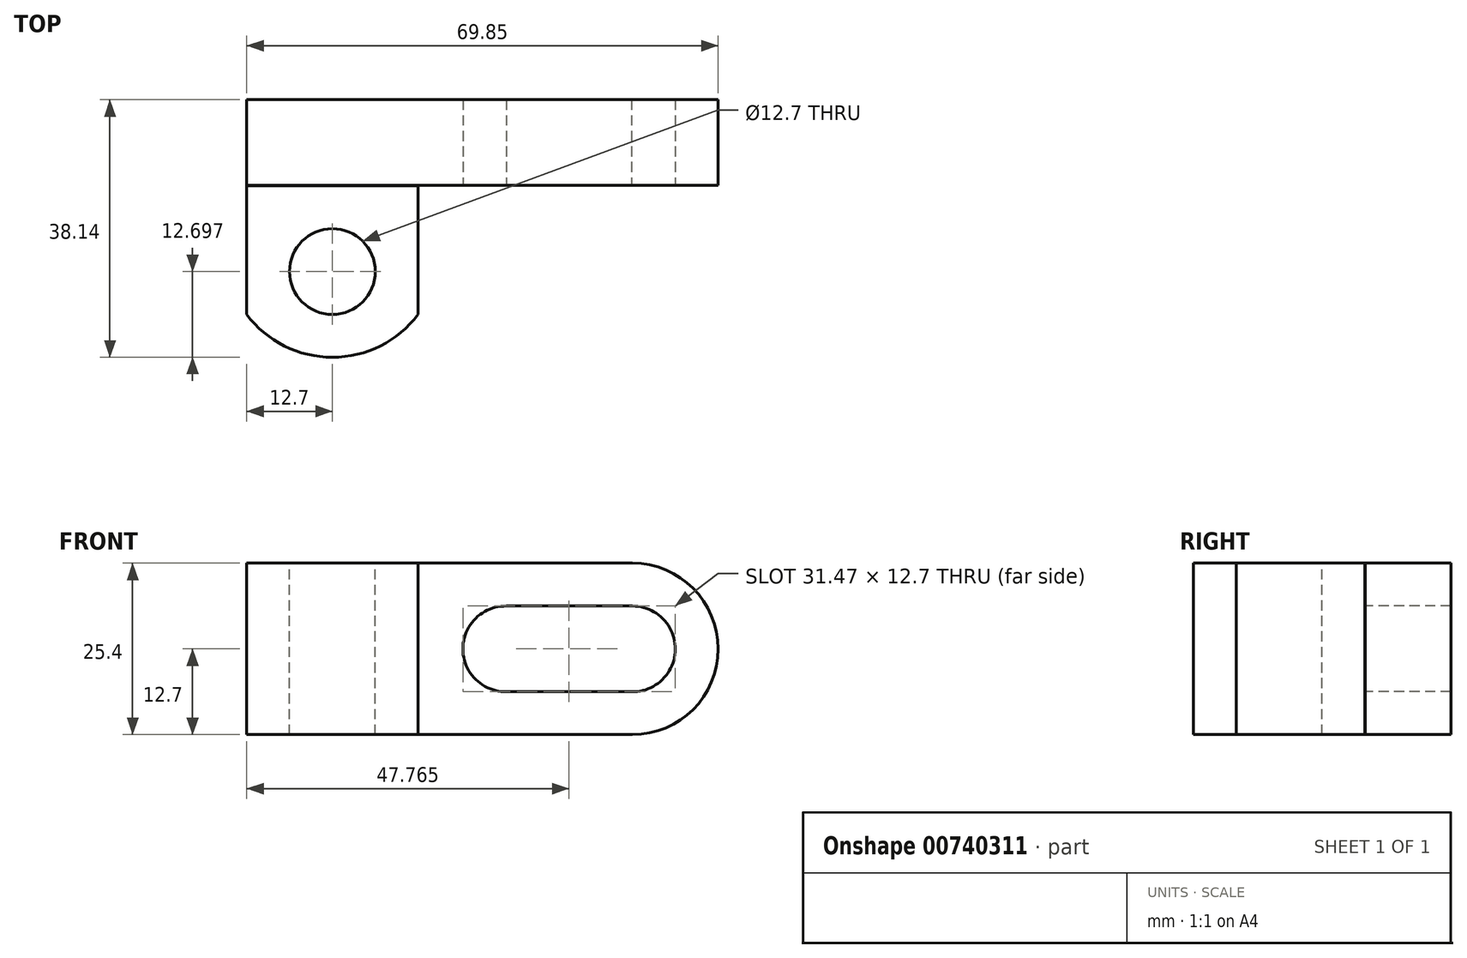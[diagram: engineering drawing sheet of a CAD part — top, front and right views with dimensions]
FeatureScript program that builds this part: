
annotation { "Feature Type Name" : "Feature", "Feature Type Description" : "" }
export const myFeature = defineFeature(function(context is Context, id is Id, definition is map)
    precondition{}
    {
        {
            var Q0;
            Q0=qCreatedBy(makeId("Front.planeOp"),FACE);
            var sketch = newSketch(context, id + "F0", { "sketchPlane" : qUnion([Q0])});
            skCircle(sketch, "E0", {"center": v(57.15, 0) * mm, "radius": 12.7 * mm});
            skLineSegment(sketch, "E1", {"start": v(57.15, 12.7) * mm, "end": v(0, 12.7) * mm});
            skLineSegment(sketch, "E2", {"start": v(0, 12.7) * mm, "end": v(0, -12.7) * mm});
            skLineSegment(sketch, "E3", {"start": v(0, -12.7) * mm, "end": v(57.15, -12.7) * mm});
            skSolve(sketch);
        }
        {
            var Q0;
            Q0 = qSketchRegion(id + "F0", true);
            extrude(context, id + "F1", {"entities" : qUnion([Q0]), "depth" : 12.7 * mm, "offsetDistance" : 25.4 * mm});
        }
        {
            var Q0;
            Q0=qCreatedBy(makeId("Top.planeOp"),FACE);
            var sketch = newSketch(context, id + "F2", { "sketchPlane" : qUnion([Q0])});
            skLineSegment(sketch, "E4", {"start": v(0, -12.74) * mm, "end": v(0, -31.8) * mm});
            skLineSegment(sketch, "E5", {"start": v(0, -31.8) * mm, "end": v(25.4, -31.8) * mm});
            skLineSegment(sketch, "E6", {"start": v(25.4, -31.8) * mm, "end": v(25.4, -12.75) * mm});
            skArc(sketch, "E7", {"start": v(0, -31.8) * mm, "mid": v(12.7, -38.14) * mm, "end": v(25.4, -31.8) * mm});
            skLineSegment(sketch, "E8", {"start": v(0, -12.74) * mm, "end": v(25.4, -12.75) * mm});
            skSolve(sketch);
        }
        {
            var Q0;
            Q0 = qSketchRegion(id + "F2", true);
            extrude(context, id + "F3", {"entities" : qUnion([Q0]), "depth" : 12.7 * mm, "offsetDistance" : 25.4 * mm});
        }
        {
            var Q0;
            Q0=makeQuery(id+"F3.opExtrude","CAP_FACE",FACE,{"disambiguationData":[OSD([sQuery(id+"F2.wireOp",EDGE,"E5"),sQuery(id+"F2.wireOp",EDGE,"E7")])],"isStart":true});
            extrude(context, id + "F4", {"entities" : qUnion([Q0]), "operationType" : NewBodyOperationType.ADD, "depth" : 12.7 * mm, "offsetDistance" : 25.4 * mm});
        }
        {
            var Q0;
            Q0 = qSketchRegion(id + "F2", true);
            extrude(context, id + "F5", {"entities" : qUnion([Q0]), "operationType" : NewBodyOperationType.ADD, "oppositeDirection" : true, "depth" : 25.4 * mm, "offsetDistance" : 25.4 * mm});
        }
        {
            var Q0;
            Q0 = qSketchRegion(id + "F2", true);
            extrude(context, id + "F6", {"entities" : qUnion([Q0]), "operationType" : NewBodyOperationType.ADD, "oppositeDirection" : true, "depth" : 12.7 * mm, "offsetDistance" : 25.4 * mm});
        }
        {
            var Q0;
            Q0=makeQuery(id+"F5.opExtrude","CAP_FACE",FACE,{"disambiguationData":[OSD([sQuery(id+"F2.wireOp",EDGE,"E4"),sQuery(id+"F2.wireOp",EDGE,"E6"),sQuery(id+"F2.wireOp",EDGE,"E7"),sQuery(id+"F2.wireOp",EDGE,"E8")])],"isStart":false});
            var sketch = newSketch(context, id + "F7", { "sketchPlane" : qUnion([Q0])});
            skSolve(sketch);
        }
        {
            var Q0;
            Q0=makeQuery(id+"F7.imprint","IMPRINT",FACE,{"disambiguationData":[TD([[makeQuery(id+"F7.imprint","IMPRINT",EDGE,{"derivedFrom":makeQuery(id+"F5.opExtrude","CAP_EDGE",EDGE,{"disambiguationData":[OSD([sQuery(id+"F2.wireOp",EDGE,"E4")])],"isStart":false})}),-1.0]])]});
            extrude(context, id + "F8", {"entities" : qUnion([Q0]), "operationType" : NewBodyOperationType.REMOVE, "oppositeDirection" : true, "depth" : 12.7 * mm, "offsetDistance" : 25.4 * mm});
        }
        {
            var Q0;
            Q0=makeQuery(id+"F1.opExtrude","CAP_FACE",FACE,{"disambiguationData":[OSD([sQuery(id+"F0.wireOp",EDGE,"E0"),sQuery(id+"F0.wireOp",EDGE,"E1"),sQuery(id+"F0.wireOp",EDGE,"E2"),sQuery(id+"F0.wireOp",EDGE,"E3")])],"isStart":false});
            var sketch = newSketch(context, id + "F9", { "sketchPlane" : qUnion([Q0])});
            skCircle(sketch, "E9", {"center": v(57.15, 0) * mm, "radius": 6.35 * mm});
            skCircle(sketch, "E10", {"center": v(38.38, 0) * mm, "radius": 6.35 * mm});
            skLineSegment(sketch, "E11", {"start": v(38.27, 6.35) * mm, "end": v(57.15, 6.35) * mm});
            skLineSegment(sketch, "E12", {"start": v(38.5, -6.35) * mm, "end": v(57.27, -6.35) * mm});
            skSolve(sketch);
        }
        {
            var Q0;
            Q0 = qSketchRegion(id + "F9", true);
            extrude(context, id + "F10", {"entities" : qUnion([Q0]), "operationType" : NewBodyOperationType.REMOVE, "endBound" : BoundingType.THROUGH_ALL, "oppositeDirection" : true, "depth" : 25.4 * mm, "offsetDistance" : 25.4 * mm});
        }
        {
            var Q0;
            Q0=qCreatedBy(makeId("Top.planeOp"),FACE);
            var sketch = newSketch(context, id + "F11", { "sketchPlane" : qUnion([Q0])});
            skCircle(sketch, "E13", {"center": v(12.7, -25.44) * mm, "radius": 6.35 * mm});
            skSolve(sketch);
        }
        {
            var Q0;
            Q0 = qSketchRegion(id + "F11", true);
            extrude(context, id + "F12", {"entities" : qUnion([Q0]), "operationType" : NewBodyOperationType.REMOVE, "endBound" : BoundingType.THROUGH_ALL, "oppositeDirection" : true, "depth" : 25.4 * mm, "offsetDistance" : 25.4 * mm});
        }
        {
            var Q0;
            Q0=qCreatedBy(makeId("Top.planeOp"),FACE);
            var sketch = newSketch(context, id + "F13", { "sketchPlane" : qUnion([Q0])});
            skCircle(sketch, "E14", {"center": v(12.7, -25.44) * mm, "radius": 6.35 * mm});
            skSolve(sketch);
        }
        {
            var Q0;
            Q0 = qSketchRegion(id + "F13", true);
            extrude(context, id + "F14", {"entities" : qUnion([Q0]), "operationType" : NewBodyOperationType.REMOVE, "endBound" : BoundingType.THROUGH_ALL, "oppositeDirection" : true, "depth" : 25.4 * mm, "offsetDistance" : 25.4 * mm});
        }
        {
            var Q0;
            Q0 = qSketchRegion(id + "F13", true);
            extrude(context, id + "F15", {"entities" : qUnion([Q0]), "operationType" : NewBodyOperationType.REMOVE, "endBound" : BoundingType.THROUGH_ALL, "depth" : 25.4 * mm, "offsetDistance" : 25.4 * mm});
        }
    });
